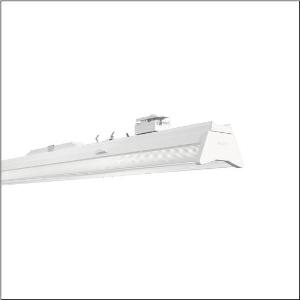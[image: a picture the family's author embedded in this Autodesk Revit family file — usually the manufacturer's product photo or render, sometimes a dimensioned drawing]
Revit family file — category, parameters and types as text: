
# Revit family: licross_r__21_performance_ho_52td16mn4e5m_6ed4
name_source: partatom
category: Lighting Fixtures
units: mm (PartAtom-declared; Revit-internal decimal feet)

## family parameters
Cut with Voids When Loaded = No
Host = Face
Light Source = No
Part Type = Normal
Room Calculation Point = No
Round Connector Dimension = Use Diameter
Shared = No

## types (1)
- --- (1 x LED, 14970 lm, 83.2 W, 4000K)
    Apparent Load = 83 VA
    CIE Flux Codes = 63 87 95 78 100
    Color Rendering = 80
    Color Temperature = 4000K
    Default Elevation = 1800 mm
    Description = Licross® 21 Performance HO, luminaire insert, of sheet steel, galvanised, coil coated, white, length: 1.500mm, width: 120mm, height: 123mm, LED rated luminous flux: 14.970lm, light colour: 840, control gear: ON/OFF Multilumen, with plug, 3-pole, with phase selection, mains connection: 220..240V, AC, 50/60Hz, rated input power: 83W, halogen-free wiring, primary light control with lens, of plastic, primary optical cover: cover, of PMMA, light emission: direct/indirect distribution, primary light characteristic: symmetric, protection rating (complete): IP54, insulation class (complete): insulation class I (protective earthing), certification: CE, ENEC, UKCA, protection symbol: D if used in an environment with non-conductive dust loads with corresponding accessories, impact resistance: IK06, permissible ambient temperature for indoor applications: -35..+35°C, corresponds to IFS (International Featured Standards) requirements for safety and quality in the food industry, reducing of maximum allowable ambient temperature of 5°C with ceiling mounting, LABS conformity tested according to VDMA 24364:2018-05, packaging unit: 1 piece
    Height = 114 mm
    Lamp = 1 x LED
    Lamp Light Flux = 14970 lm
    Lamp Power = 83.2 W
    Lamp count = 1
    Length = 1500 mm
    Luminous efficacy = 180 lm/W
    Manufacturer = Siteco
    ModVariant = No
    Model = 52TD16MN4E5M
    Mounting Place = Ceiling
    Mounting Type = Pendant
    Number of Poles = 1
    OnlyDefault = Yes
    Power Factor = 1
    Product Name = Licross® 21 Performance HO
    Product group = luminaire insert
    ProductGroupID = 901
    Protection Class = Protection class I
    Protection Degree = IP 54
    RLX_Detail_Level = 1
    RLX_Emergency_Light_Flux = 0 lm
    RLX_Emergency_Type = 0
    RLX_Emergency_Type_DB = No
    RlxData = <blob elided: 31793 chars, md5=aba42142>
    Socket = socket
    Standby Power = 0 W
    System Light Flux = 14970 lm
    System Power = 83 W
    Type Comments = factory setting: luminous flux: 100 % | (A | C | E) | 195 mA
    Type Image = l_1256138.jpg
    URL = http://relux.com
    VarID = @adj_057525
    Voltage = 0 V
    Weight = 0.00 kg
    Width = 120 mm

## geometry (parser evidence)
native form markers: Blend x4, Sweep x13
no freeform markers — native parametric forms only
